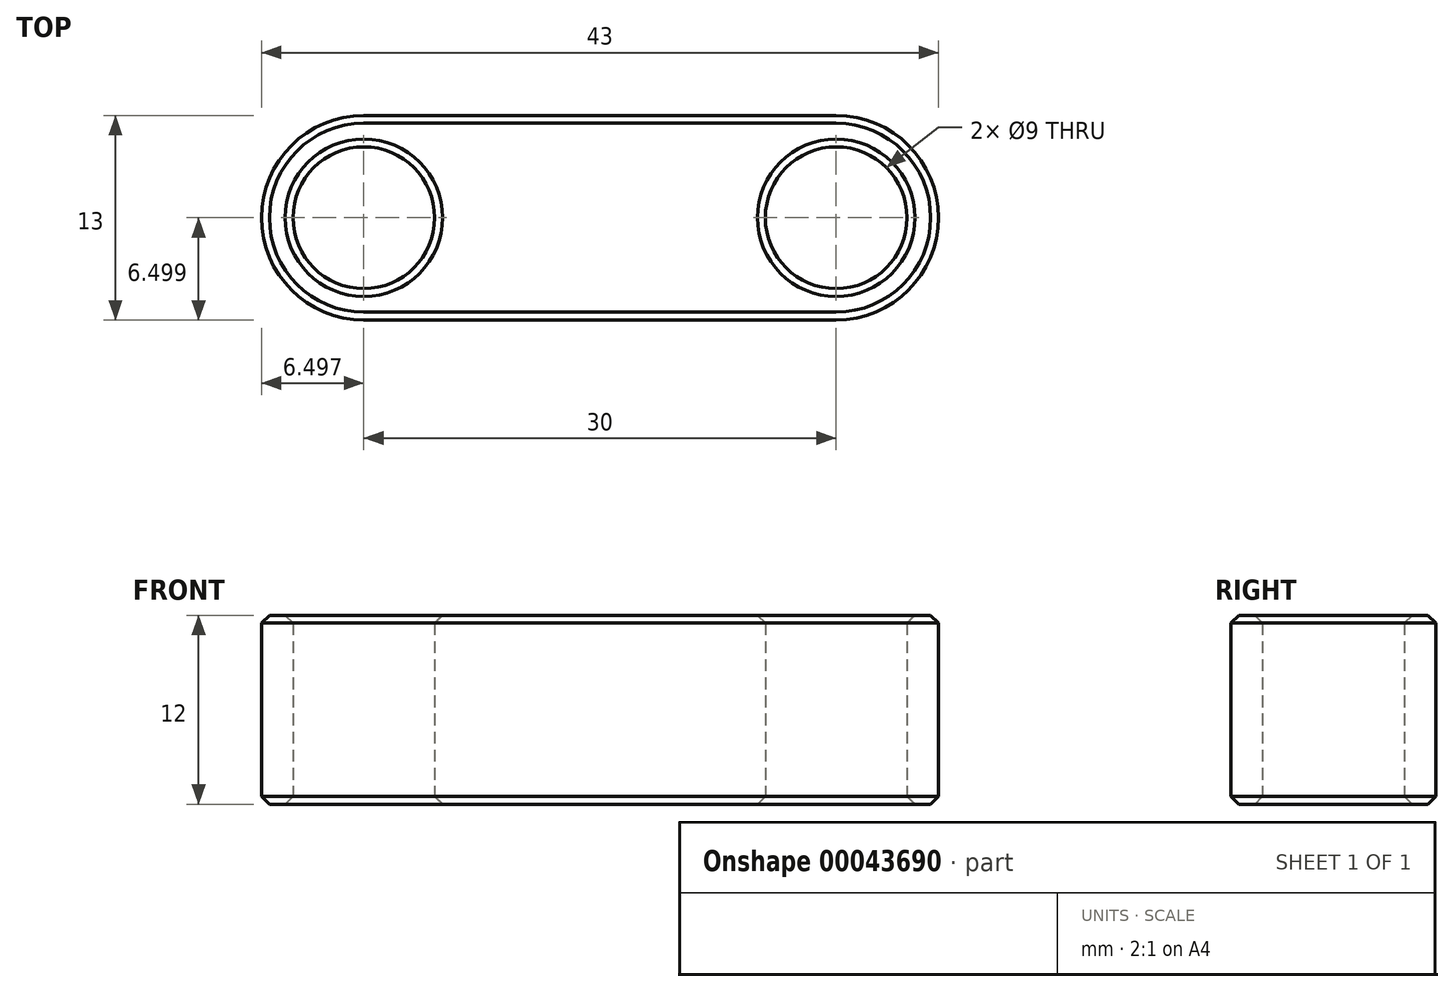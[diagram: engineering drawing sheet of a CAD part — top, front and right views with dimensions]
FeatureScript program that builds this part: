
annotation { "Feature Type Name" : "Feature", "Feature Type Description" : "" }
export const myFeature = defineFeature(function(context is Context, id is Id, definition is map)
    precondition{}
    {
        {
            var Q0;
            Q0=qCreatedBy(makeId("Top.planeOp"),FACE);
            var sketch = newSketch(context, id + "F0", { "sketchPlane" : qUnion([Q0])});
            skLineSegment(sketch, "E0.bottom", {"start": v(-11.6, 5.59) * mm, "end": v(18.4, 5.59) * mm});
            skLineSegment(sketch, "E0.top", {"start": v(-11.6, -7.41) * mm, "end": v(18.4, -7.41) * mm});
            skLineSegment(sketch, "E0.left", {"start": v(-11.6, 5.59) * mm, "end": v(-11.6, -7.41) * mm});
            skLineSegment(sketch, "E0.right", {"start": v(18.4, 5.59) * mm, "end": v(18.4, -7.41) * mm});
            skCircle(sketch, "E1", {"center": v(-11.6, -0.91) * mm, "radius": 6.5 * mm});
            skCircle(sketch, "E2", {"center": v(18.4, -0.91) * mm, "radius": 6.5 * mm});
            skCircle(sketch, "E3", {"center": v(-11.6, -0.91) * mm, "radius": 4.5 * mm});
            skLineSegment(sketch, "E4", {"start": v(-11.6, -5.41) * mm, "end": v(18.4, -5.41) * mm});
            skCircle(sketch, "E5", {"center": v(18.4, -0.91) * mm, "radius": 4.5 * mm});
            skSolve(sketch);
        }
        {
            var Q0;
            {var subQ0=sQuery(id+"F0.wireOp",EDGE,"E3");var subQ1=sQuery(id+"F0.wireOp",EDGE,"E0.left");var subQ2=makeQuery(id+"F0.imprint","INTERSECT",VERTEX,{"derivedFrom":[subQ1,subQ0]});Q0=makeQuery(id+"F0.imprint","IMPRINT",FACE,{"disambiguationData":[TD([[makeQuery(id+"F0.imprint","IMPRINT",EDGE,{"disambiguationData":[TD([[subQ2,1.0]])],"derivedFrom":subQ1}),-1.0]])]});}
            var Q1;
            {var subQ0=sQuery(id+"F0.wireOp",EDGE,"E3");var subQ1=sQuery(id+"F0.wireOp",EDGE,"E0.left");var subQ2=makeQuery(id+"F0.imprint","INTERSECT",VERTEX,{"derivedFrom":[subQ1,subQ0]});Q1=makeQuery(id+"F0.imprint","IMPRINT",FACE,{"disambiguationData":[TD([[makeQuery(id+"F0.imprint","IMPRINT",EDGE,{"disambiguationData":[TD([[subQ2,1.0]])],"derivedFrom":subQ1}),1.0]])]});}
            var Q2;
            {var subQ3=sQuery(id+"F0.wireOp",EDGE,"E0.bottom");Q2=makeQuery(id+"F0.imprint","IMPRINT",FACE,{"disambiguationData":[TD([[makeQuery(id+"F0.imprint","IMPRINT",EDGE,{"derivedFrom":subQ3}),-1.0]])]});}
            var Q3;
            {var subQ3=sQuery(id+"F0.wireOp",EDGE,"E0.right");var subQ4=sQuery(id+"F0.wireOp",EDGE,"E5");var subQ7=makeQuery(id+"F0.imprint","INTERSECT",VERTEX,{"derivedFrom":[subQ3,subQ4]});Q3=makeQuery(id+"F0.imprint","IMPRINT",FACE,{"disambiguationData":[TD([[makeQuery(id+"F0.imprint","IMPRINT",EDGE,{"disambiguationData":[TD([[subQ7,1.0]])],"derivedFrom":subQ3}),-1.0]])]});}
            var Q4;
            {var subQ1=sQuery(id+"F0.wireOp",EDGE,"E0.right");var subQ4=sQuery(id+"F0.wireOp",EDGE,"E5");var subQ5=makeQuery(id+"F0.imprint","INTERSECT",VERTEX,{"derivedFrom":[subQ1,subQ4]});Q4=makeQuery(id+"F0.imprint","IMPRINT",FACE,{"disambiguationData":[TD([[makeQuery(id+"F0.imprint","IMPRINT",EDGE,{"disambiguationData":[TD([[subQ5,1.0]])],"derivedFrom":subQ1}),1.0]])]});}
            var Q5;
            {var subQ0=sQuery(id+"F0.wireOp",EDGE,"E4");var subQ1=sQuery(id+"F0.wireOp",EDGE,"E2");var subQ2=makeQuery(id+"F0.imprint","INTERSECT",VERTEX,{"derivedFrom":[subQ1,subQ0]});Q5=makeQuery(id+"F0.imprint","IMPRINT",FACE,{"disambiguationData":[TD([[makeQuery(id+"F0.imprint","IMPRINT",EDGE,{"disambiguationData":[TD([[subQ2,-1.0]])],"derivedFrom":subQ1}),1.0]])]});}
            var Q6;
            {var subQ3=sQuery(id+"F0.wireOp",EDGE,"E0.top");Q6=makeQuery(id+"F0.imprint","IMPRINT",FACE,{"disambiguationData":[TD([[makeQuery(id+"F0.imprint","IMPRINT",EDGE,{"derivedFrom":subQ3}),1.0]])]});}
            var Q7;
            {var subQ0=sQuery(id+"F0.wireOp",EDGE,"E4");var subQ1=sQuery(id+"F0.wireOp",EDGE,"E1");var subQ2=makeQuery(id+"F0.imprint","INTERSECT",VERTEX,{"derivedFrom":[subQ1,subQ0]});Q7=makeQuery(id+"F0.imprint","IMPRINT",FACE,{"disambiguationData":[TD([[makeQuery(id+"F0.imprint","IMPRINT",EDGE,{"disambiguationData":[TD([[subQ2,1.0]])],"derivedFrom":subQ1}),1.0]])]});}
            extrude(context, id + "F1", {"entities" : qUnion([Q0, Q1, Q2, Q3, Q4, Q5, Q6, Q7]), "depth" : 12 * mm});
        }
        {
            var Q0;
            Q0=makeQuery(id+"F1.opExtrude","CAP_EDGE",EDGE,{"disambiguationData":[OSD([sQuery(id+"F0.wireOp",EDGE,"E1")])],"isStart":false});
            var Q1;
            Q1=makeQuery(id+"F1.opExtrude","CAP_EDGE",EDGE,{"disambiguationData":[OSD([sQuery(id+"F0.wireOp",EDGE,"E0.top")])],"isStart":false});
            var Q2;
            Q2=makeQuery(id+"F1.opExtrude","CAP_FACE",FACE,{"disambiguationData":[OSD([sQuery(id+"F0.wireOp",EDGE,"E0.bottom"),sQuery(id+"F0.wireOp",EDGE,"E0.top"),sQuery(id+"F0.wireOp",EDGE,"E1"),sQuery(id+"F0.wireOp",EDGE,"E2"),sQuery(id+"F0.wireOp",EDGE,"E3"),sQuery(id+"F0.wireOp",EDGE,"E5")])],"isStart":false});
            var Q3;
            Q3=makeQuery(id+"F1.opExtrude","CAP_FACE",FACE,{"disambiguationData":[OSD([sQuery(id+"F0.wireOp",EDGE,"E0.bottom"),sQuery(id+"F0.wireOp",EDGE,"E0.top"),sQuery(id+"F0.wireOp",EDGE,"E1"),sQuery(id+"F0.wireOp",EDGE,"E2"),sQuery(id+"F0.wireOp",EDGE,"E3"),sQuery(id+"F0.wireOp",EDGE,"E5")])],"isStart":true});
            chamfer(context, id + "F2", {"entities" : qUnion([Q0, Q1, Q2, Q3]), "width" : 0.5 * mm, "tangentPropagation" : true});
        }
        {
            var Q0;
            Q0=makeQuery(id+"F1.opExtrude","SWEPT_BODY",BODY,{"disambiguationData":[OSD([sQuery(id+"F0.wireOp",EDGE,"E0.bottom"),sQuery(id+"F0.wireOp",EDGE,"E0.top"),sQuery(id+"F0.wireOp",EDGE,"E1"),sQuery(id+"F0.wireOp",EDGE,"E2"),sQuery(id+"F0.wireOp",EDGE,"E3"),sQuery(id+"F0.wireOp",EDGE,"E5")])]});
            transform(context, id + "F3", {"entities" : qUnion([Q0]), "transformType" : TransformType.TRANSLATION_3D, "dx" : 0 * mm, "dy" : -24.46 * mm, "dz" : 0 * mm, "makeCopy" : true});
        }
        {
            var Q0;
            Q0=makeQuery(id+"F3.opPattern","COPY",BODY,{"derivedFrom":makeQuery(id+"F1.opExtrude","SWEPT_BODY",BODY,{"disambiguationData":[OSD([sQuery(id+"F0.wireOp",EDGE,"E0.bottom"),sQuery(id+"F0.wireOp",EDGE,"E0.top"),sQuery(id+"F0.wireOp",EDGE,"E1"),sQuery(id+"F0.wireOp",EDGE,"E2"),sQuery(id+"F0.wireOp",EDGE,"E3"),sQuery(id+"F0.wireOp",EDGE,"E5")])]}),"instanceName":"1"});
            deleteBodies(context, id + "F4", {"entities" : qUnion([Q0])});
        }
    });
